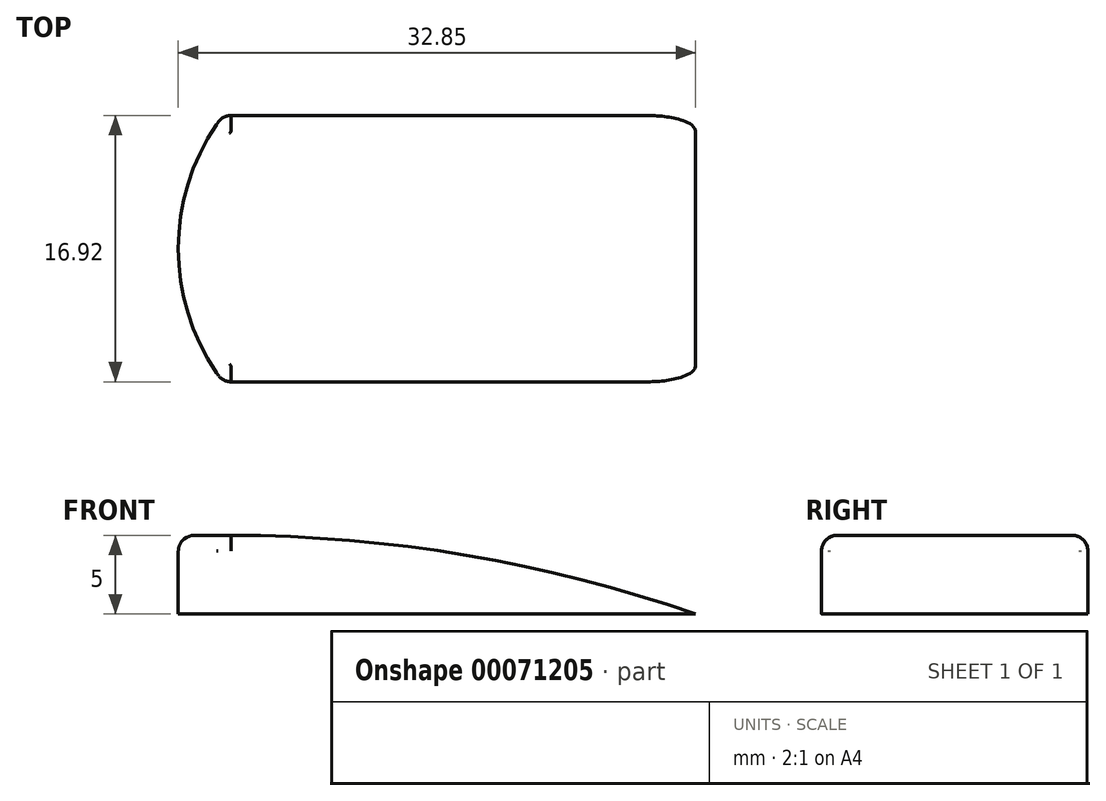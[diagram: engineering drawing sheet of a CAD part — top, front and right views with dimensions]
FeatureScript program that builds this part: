
annotation { "Feature Type Name" : "Feature", "Feature Type Description" : "" }
export const myFeature = defineFeature(function(context is Context, id is Id, definition is map)
    precondition{}
    {
        {
            var Q0;
            Q0=qCreatedBy(makeId("Top.planeOp"),FACE);
            var sketch = newSketch(context, id + "F0", { "sketchPlane" : qUnion([Q0])});
            skArc(sketch, "E0", {"start": v(11.65, 8.46) * mm, "mid": v(8.8, 0) * mm, "end": v(11.65, -8.46) * mm});
            skPoint(sketch, "E1.endSnap0", {"position": v(140.65, 0) * mm});
            skPoint(sketch, "E2.oppositeSnap0", {"position": v(24.14, -8.46) * mm});
            skLineSegment(sketch, "E2.bottom", {"start": v(11.65, 8.46) * mm, "end": v(41.65, 8.46) * mm});
            skLineSegment(sketch, "E2.top", {"start": v(11.65, -8.46) * mm, "end": v(41.65, -8.46) * mm});
            skLineSegment(sketch, "E2.right", {"start": v(41.65, 8.46) * mm, "end": v(41.65, -8.46) * mm});
            skSolve(sketch);
        }
        {
            var Q0;
            Q0 = qSketchRegion(id + "F0", true);
            extrude(context, id + "F1", {"entities" : qUnion([Q0]), "depth" : 5 * mm});
        }
        {
            var Q0;
            Q0=makeQuery(id+"F1.opExtrude","CAP_EDGE",EDGE,{"disambiguationData":[OSD([sQuery(id+"F0.wireOp",EDGE,"E2.right")])],"isStart":false});
            fillet(context, id + "F2", {"entities" : qUnion([Q0]), "radius" : 90 * mm, "tangentPropagation" : true, "allowEdgeOverflow" : false});
        }
        {
            var Q0;
            Q0=makeQuery(id+"F2.opFillet","BLEND_EDGE",EDGE,{"blendedFrom":[makeQuery(id+"F1.opExtrude","CAP_EDGE",EDGE,{"disambiguationData":[OSD([sQuery(id+"F0.wireOp",EDGE,"E2.right")])],"isStart":false}),makeQuery(id+"F1.opExtrude","SWEPT_FACE",FACE,{"disambiguationData":[OSD([sQuery(id+"F0.wireOp",EDGE,"E2.top")])]})],"blendedInto":[makeQuery(id+"F1.opExtrude","SWEPT_FACE",FACE,{"disambiguationData":[OSD([sQuery(id+"F0.wireOp",EDGE,"E2.top")])]})]});
            var Q1;
            Q1=makeQuery(id+"F2.opFillet","BLEND_EDGE",EDGE,{"blendedFrom":[makeQuery(id+"F1.opExtrude","CAP_EDGE",EDGE,{"disambiguationData":[OSD([sQuery(id+"F0.wireOp",EDGE,"E2.right")])],"isStart":false}),makeQuery(id+"F1.opExtrude","SWEPT_FACE",FACE,{"disambiguationData":[OSD([sQuery(id+"F0.wireOp",EDGE,"E2.bottom")])]})],"blendedInto":[makeQuery(id+"F1.opExtrude","SWEPT_FACE",FACE,{"disambiguationData":[OSD([sQuery(id+"F0.wireOp",EDGE,"E2.bottom")])]})]});
            var Q2;
            Q2=makeQuery(id+"F1.opExtrude","CAP_EDGE",EDGE,{"disambiguationData":[OSD([sQuery(id+"F0.wireOp",EDGE,"E0")])],"isStart":false});
            fillet(context, id + "F3", {"entities" : qUnion([Q0, Q1, Q2]), "radius" : 1 * mm, "tangentPropagation" : true, "allowEdgeOverflow" : false});
        }
        {
            var Q0;
            Q0=makeQuery(id+"F1.opExtrude","SWEPT_EDGE",EDGE,{"disambiguationData":[OSD([sQuery(id+"F0.wireOp",EDGE,"E0"),sQuery(id+"F0.wireOp",EDGE,"E2.bottom")])]});
            var Q1;
            Q1=makeQuery(id+"F1.opExtrude","SWEPT_EDGE",EDGE,{"disambiguationData":[OSD([sQuery(id+"F0.wireOp",EDGE,"E0"),sQuery(id+"F0.wireOp",EDGE,"E2.top")])]});
            fillet(context, id + "F4", {"entities" : qUnion([Q0, Q1]), "radius" : 1 * mm, "tangentPropagation" : true, "allowEdgeOverflow" : false});
        }
    });
